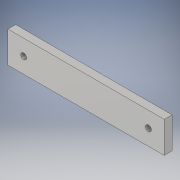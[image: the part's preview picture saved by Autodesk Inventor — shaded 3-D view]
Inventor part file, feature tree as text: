
AUTODESK INVENTOR PART (.ipt)
format: ipt  version: 2019 (Build 230136000, 136)  size: 115,200 bytes
history: native  units: in
note: dims shown in document units (in); Inventor stores cm internally (conversion verified against a paired STEP export)
features: extrude x2, sketch x2, plane x1, mirror x1
ambient origin geometry x8: Origin, YZ Plane, XZ Plane, XY Plane, X Axis, Y Axis, Z Axis, Center Point
bodies: Solid1 (feature_tree)
feature tree (6):
  extrude  "Extrusion1"  Depth=1.0in
  extrude  "Extrusion2"  Depth=0.25in
  plane  "Work Plane1"
  mirror  "Mirror1"
  sketch  "Sketch1"  dims[d0=5.0in d1=1.0in]
  sketch  "Sketch2"  dims[d2=0.25in d3=0.0in d4=0.5in d5=0.5034in d6=0.1875in d7=0.25in d8=0.0in]
